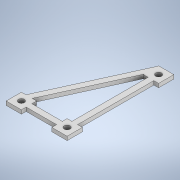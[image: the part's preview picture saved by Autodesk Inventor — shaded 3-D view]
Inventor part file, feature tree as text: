
AUTODESK INVENTOR PART (.ipt)
format: ipt  version: 2020 (Build 240168000, 168)  size: 158,208 bytes
history: native  units: mm
features: sketch x2, other x1, extrude x1
ambient origin geometry x8: Origin, YZ Plane, XZ Plane, XY Plane, X Axis, Y Axis, Z Axis, Center Point
bodies: Solid1 (feature_tree)
feature tree (4):
  other  "HexBodyV2.ipt"
  extrude  "Extrusion1"  Depth=10.0mm
  sketch  "Sketch14"  dims[d2=3.1mm d3=3.1mm d4=3.0mm d5=3.0mm d6=3.0mm d7=2.0mm d8=0.0mm]
  sketch  "Sketch2"  dims[d0=10.0mm d1=3.1mm]
